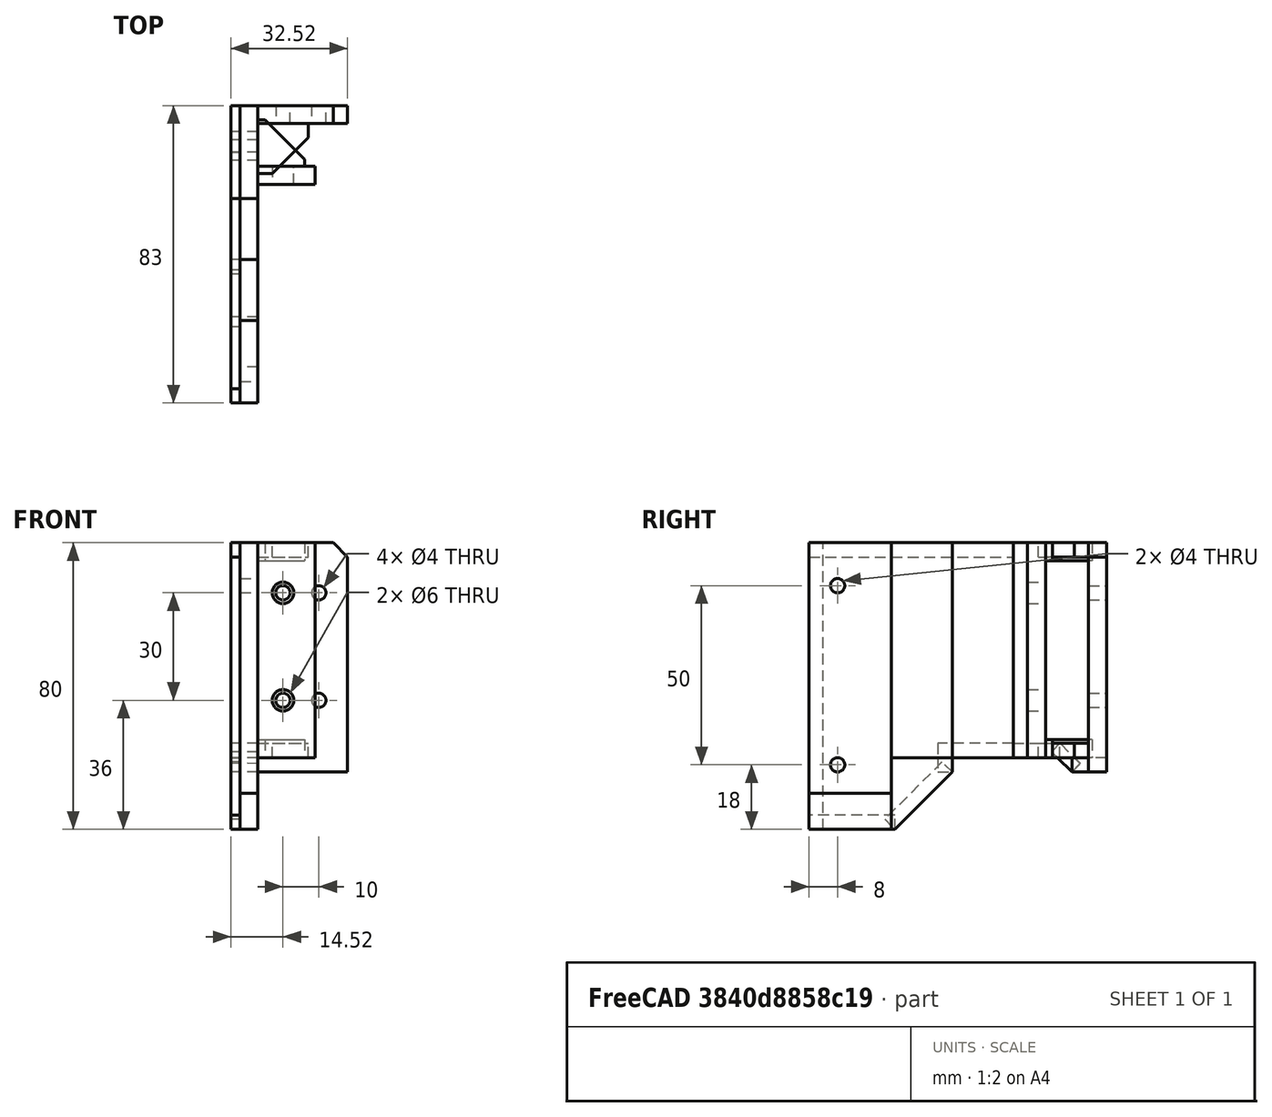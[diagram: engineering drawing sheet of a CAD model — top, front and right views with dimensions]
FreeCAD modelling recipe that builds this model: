
FCSTD DOCUMENT  (FreeCAD 0.20R29410 (Git))
Label: main_02
License: All rights reserved
LicenseURL: http://en.wikipedia.org/wiki/All_rights_reserved
objects: Part::Part2DObjectPython×35, Part::Extrusion×30, Part::Mirroring×22, Part::Cut×8, Part::Chamfer×6, App::FeaturePython×1
note: 101 computed .brp shape members not serialized (recipe doc carries the construction recipe); baked Part::Feature solids carry a one-line shape summary decoded from their .brp

FEATURE [Part::Part2DObjectPython] Rectangle  # Draft 2D object (typed FeaturePython)
  Area = 0
  ChamferSize = 0
  Columns = 1
  FilletRadius = 0
  Height = 70
  Length = 23
  MakeFace = false
  Placement = pos=(0,-40,0) rot=(0.57735,0.57735,0.57735;2.0944rad)
  Rows = 1
FEATURE [Part::Part2DObjectPython] Circle  # Draft 2D object (typed FeaturePython)
  Area = 0
  FirstAngle = 0
  LastAngle = 0
  MakeFace = false
  Placement = pos=(0,-32,58) rot=(0.57735,0.57735,0.57735;2.0944rad)
  Radius = 4
FEATURE [Part::Part2DObjectPython] Circle001  # Draft 2D object (typed FeaturePython)
  Area = 0
  FirstAngle = 0
  LastAngle = 0
  MakeFace = false
  Placement = pos=(0,-32,8) rot=(0.57735,0.57735,0.57735;2.0944rad)
  Radius = 4
FEATURE [Part::Part2DObjectPython] Rectangle001  # Draft 2D object (typed FeaturePython)
  Area = 0
  ChamferSize = 0
  Columns = 1
  FilletRadius = 0
  Height = 10
  Length = 23
  MakeFace = false
  Placement = pos=(0,-40,-10) rot=(0.57735,0.57735,0.57735;2.0944rad)
  Rows = 1
FEATURE [Part::Part2DObjectPython] Rectangle002  # Draft 2D object (typed FeaturePython)
  Area = 0
  ChamferSize = 0
  Columns = 1
  FilletRadius = 0
  Height = 20
  Length = 17
  MakeFace = false
  Placement = pos=(0,-17,-10) rot=(0.57735,0.57735,0.57735;2.0944rad)
  Rows = 1
FEATURE [Part::Part2DObjectPython] Rectangle003  # Draft 2D object (typed FeaturePython)
  Area = 0
  ChamferSize = 0
  Columns = 1
  FilletRadius = 0
  Height = 60
  Length = 17
  MakeFace = false
  Placement = pos=(0,0,10) rot=(0.57735,0.57735,0.57735;2.0944rad)
  Rows = 1
FEATURE [Part::Part2DObjectPython] Rectangle004  # Draft 2D object (typed FeaturePython)
  Area = 0
  ChamferSize = 0
  Columns = 1
  FilletRadius = 0
  Height = 60
  Length = 17
  MakeFace = false
  Placement = pos=(0,-17,10) rot=(0.57735,0.57735,0.57735;2.0944rad)
  Rows = 1
FEATURE [Part::Extrusion] Extrude
  Base = -> Rectangle
  Dir = (1,-2e-16,2e-16)
  DirMode = 2
  FaceMakerClass = Part::FaceMakerBullseye
  LengthFwd = 5
  LengthRev = 0
  Solid = true
  Symmetric = false
FEATURE [Part::Extrusion] Extrude001
  Base = -> Rectangle004
  Dir = (1,0,0)
  DirMode = 2
  FaceMakerClass = Part::FaceMakerBullseye
  LengthFwd = 5
  LengthRev = 0
  Solid = true
  Symmetric = false
FEATURE [Part::Extrusion] Extrude002
  Base = -> Rectangle003
  Dir = (1,-2e-16,2e-16)
  DirMode = 2
  FaceMakerClass = Part::FaceMakerBullseye
  LengthFwd = 5
  LengthRev = 0
  Solid = true
  Symmetric = false
FEATURE [Part::Extrusion] Extrude003
  Base = -> Rectangle001
  Dir = (1,-2e-16,2e-16)
  DirMode = 2
  FaceMakerClass = Part::FaceMakerBullseye
  LengthFwd = 5
  LengthRev = 0
  Solid = true
  Symmetric = false
FEATURE [Part::Extrusion] Extrude004
  Base = -> Rectangle002
  Dir = (1,-2e-16,2e-16)
  DirMode = 2
  FaceMakerClass = Part::FaceMakerBullseye
  LengthFwd = 5
  LengthRev = 0
  Solid = true
  Symmetric = false
FEATURE [Part::Chamfer] Chamfer
  Base = -> Extrude004
  Edges = 1 edges r=16: [Edge2]
FEATURE [Part::Part2DObjectPython] Rectangle005  # Draft 2D object (typed FeaturePython)
  Area = 0
  ChamferSize = 0
  Columns = 1
  FilletRadius = 0
  Height = 4
  Length = 57
  MakeFace = false
  Placement = pos=(5,-40,66) rot=(0.57735,0.57735,0.57735;2.0944rad)
  Rows = 1
FEATURE [Part::Part2DObjectPython] Rectangle006  # Draft 2D object (typed FeaturePython)
  Area = 0
  ChamferSize = 0
  Columns = 1
  FilletRadius = 0
  Height = 80
  Length = 4
  MakeFace = false
  Placement = pos=(5,-40,-10) rot=(0.57735,0.57735,0.57735;2.0944rad)
  Rows = 1
FEATURE [Part::Part2DObjectPython] Rectangle007  # Draft 2D object (typed FeaturePython)
  Area = 0
  ChamferSize = 0
  Columns = 1
  FilletRadius = 0
  Height = 4
  Length = 24
  MakeFace = false
  Placement = pos=(5,-40,-10) rot=(0.57735,0.57735,0.57735;2.0944rad)
  Rows = 1
FEATURE [Part::Part2DObjectPython] Rectangle008  # Draft 2D object (typed FeaturePython)
  Area = 0
  ChamferSize = 0
  Columns = 1
  FilletRadius = 0
  Height = 4
  Length = 22.6
  MakeFace = false
  Placement = pos=(5,-16,-10) rot=(0.678598,0.281085,0.678598;2.59356rad)
  Rows = 1
FEATURE [Part::Part2DObjectPython] Rectangle009  # Draft 2D object (typed FeaturePython)
  Area = 0
  ChamferSize = 0
  Columns = 1
  FilletRadius = 0
  Height = 4
  Length = 4
  MakeFace = false
  Placement = pos=(5,-4,6) rot=(0.57735,0.57735,0.57735;2.0944rad)
  Rows = 1
FEATURE [Part::Part2DObjectPython] Rectangle010  # Draft 2D object (typed FeaturePython)
  Area = 0
  ChamferSize = 0
  Columns = 1
  FilletRadius = 0
  Height = 4
  Length = 21
  MakeFace = false
  Placement = pos=(5,-4,10) rot=(0.57735,0.57735,0.57735;2.0944rad)
  Rows = 1
FEATURE [Part::Extrusion] Extrude005
  Base = -> Rectangle005
  Dir = (1,-2e-16,2e-16)
  DirMode = 2
  FaceMakerClass = Part::FaceMakerBullseye
  LengthFwd = 2.5
  LengthRev = 0
  Solid = true
  Symmetric = false
FEATURE [Part::Extrusion] Extrude006
  Base = -> Rectangle006
  Dir = (1,-2e-16,2e-16)
  DirMode = 2
  FaceMakerClass = Part::FaceMakerBullseye
  LengthFwd = 2.5
  LengthRev = 0
  Solid = true
  Symmetric = false
FEATURE [Part::Extrusion] Extrude007
  Base = -> Rectangle007
  Dir = (1,-2e-16,2e-16)
  DirMode = 2
  FaceMakerClass = Part::FaceMakerBullseye
  LengthFwd = 2.5
  LengthRev = 0
  Solid = true
  Symmetric = false
FEATURE [Part::Extrusion] Extrude008
  Base = -> Rectangle008
  Dir = (1,-2.79271e-06,1.15679e-06)
  DirMode = 2
  FaceMakerClass = Part::FaceMakerBullseye
  LengthFwd = 2.5
  LengthRev = 0
  Solid = true
  Symmetric = false
FEATURE [Part::Extrusion] Extrude009
  Base = -> Rectangle009
  Dir = (1,-2e-16,2e-16)
  DirMode = 2
  FaceMakerClass = Part::FaceMakerBullseye
  LengthFwd = 2.5
  LengthRev = 0
  Solid = true
  Symmetric = false
FEATURE [Part::Extrusion] Extrude010
  Base = -> Rectangle010
  Dir = (1,-2e-16,2e-16)
  DirMode = 2
  FaceMakerClass = Part::FaceMakerBullseye
  LengthFwd = 2.5
  LengthRev = 0
  Solid = true
  Symmetric = false
FEATURE [Part::Part2DObjectPython] Rectangle011  # Draft 2D object (typed FeaturePython)
  Area = 0
  ChamferSize = 0
  Columns = 1
  FilletRadius = 0
  Height = 60
  Length = 5.00266
  MakeFace = false
  Placement = pos=(6e-15,-13,10) rot=(0.57735,-0.57735,-0.57735;2.0944rad)
  Rows = 1
FEATURE [Part::Extrusion] Extrude011
  Base = -> Rectangle011
  Dir = (-1,2e-16,-2e-16)
  DirMode = 2
  FaceMakerClass = Part::FaceMakerBullseye
  LengthFwd = 16
  LengthRev = 0
  Placement = pos=(0,37,0) rot=(0,0,1;0rad)
  Solid = true
  Symmetric = false
FEATURE [Part::Part2DObjectPython] Rectangle012  # Draft 2D object (typed FeaturePython)
  Area = 0
  ChamferSize = 0
  Columns = 1
  FilletRadius = 0
  Height = 5
  Length = 13
  MakeFace = false
  Placement = pos=(0,0,63) rot=(0.57735,-0.57735,-0.57735;2.0944rad)
  Rows = 1
FEATURE [Part::Extrusion] Extrude012
  Base = -> Rectangle012
  Dir = (-1,-2e-16,2e-16)
  DirMode = 2
  FaceMakerClass = Part::FaceMakerBullseye
  LengthFwd = 13
  LengthRev = 0
  Solid = true
  Symmetric = false
FEATURE [Part::Chamfer] Chamfer001
  Base = -> Extrude012
  Edges = 1 edges r=11: [Edge12]
  Placement = pos=(0,39,2) rot=(0,0,1;0rad)
FEATURE [Part::Part2DObjectPython] Rectangle013  # Draft 2D object (typed FeaturePython)
  Area = 0
  ChamferSize = 0
  Columns = 1
  FilletRadius = 0
  Height = 5
  Length = 13
  MakeFace = false
  Placement = pos=(0,0,63) rot=(0.57735,-0.57735,-0.57735;2.0944rad)
  Rows = 1
FEATURE [Part::Extrusion] Extrude013
  Base = -> Rectangle013
  Dir = (-1,-2e-16,2e-16)
  DirMode = 2
  FaceMakerClass = Part::FaceMakerBullseye
  LengthFwd = 13
  LengthRev = 0
  Solid = true
  Symmetric = false
FEATURE [Part::Chamfer] Chamfer002
  Base = -> Extrude013
  Edges = 1 edges r=11: [Edge12]
  Placement = pos=(0,39,-53) rot=(0,0,1;0rad)
FEATURE [Part::Part2DObjectPython] Rectangle014  # Draft 2D object (typed FeaturePython)
  Area = 0
  ChamferSize = 0
  Columns = 1
  FilletRadius = 0
  Height = 49.9966
  Length = 4
  MakeFace = false
  Placement = pos=(0,-9,15) rot=(0.57735,-0.57735,-0.57735;2.0944rad)
  Rows = 1
FEATURE [Part::Part2DObjectPython] Rectangle015  # Draft 2D object (typed FeaturePython)
  Area = 0
  ChamferSize = 0
  Columns = 1
  FilletRadius = 0
  Height = 16
  Length = 5
  MakeFace = false
  Placement = pos=(0,-13,-6) rot=(0.57735,-0.57735,-0.57735;2.0944rad)
  Rows = 1
FEATURE [Part::Part2DObjectPython] Circle002  # Draft 2D object (typed FeaturePython)
  Area = 0
  FirstAngle = 0
  LastAngle = 0
  MakeFace = false
  Placement = pos=(0,-32,58) rot=(0.57735,0.57735,0.57735;2.0944rad)
  Radius = 2
FEATURE [Part::Part2DObjectPython] Circle003  # Draft 2D object (typed FeaturePython)
  Area = 0
  FirstAngle = 0
  LastAngle = 0
  MakeFace = false
  Placement = pos=(0,-32,8) rot=(0.57735,0.57735,0.57735;2.0944rad)
  Radius = 2
FEATURE [Part::Extrusion] Extrude016
  Base = -> Circle003
  Dir = (1,0,0)
  DirMode = 2
  FaceMakerClass = Part::FaceMakerBullseye
  LengthFwd = 5
  LengthRev = 0
  Solid = true
  Symmetric = false
FEATURE [Part::Extrusion] Extrude017
  Base = -> Circle002
  Dir = (1,0,0)
  DirMode = 2
  FaceMakerClass = Part::FaceMakerBullseye
  LengthFwd = 5
  LengthRev = 0
  Solid = true
  Symmetric = false
FEATURE [Part::Cut] Cut
  Base = -> Extrude
  Tool = -> Extrude016
FEATURE [Part::Cut] Cut001
  Base = -> Cut
  Tool = -> Extrude017
FEATURE [Part::Part2DObjectPython] Rectangle016  # Draft 2D object (typed FeaturePython)
  Area = 300
  ChamferSize = 0
  Columns = 1
  FilletRadius = 0
  Height = 60
  Length = 5
  MakeFace = true
  Placement = pos=(5,17,10) rot=(0,0.707107,0.707107;3.14159rad)
  Rows = 1
FEATURE [Part::Extrusion] Extrude018
  Base = -> Rectangle016
  Dir = (1e-16,1,0)
  DirMode = 2
  FaceMakerClass = Part::FaceMakerBullseye
  LengthFwd = 26
  LengthRev = 0
  Solid = false
  Symmetric = false
FEATURE [Part::Part2DObjectPython] Rectangle017  # Draft 2D object (typed FeaturePython)
  Area = 10
  ChamferSize = 0
  Columns = 1
  FilletRadius = 0
  Height = 4
  Length = 2.5
  MakeFace = true
  Placement = pos=(7.5,17,66) rot=(0,0.707107,0.707107;3.14159rad)
  Rows = 1
FEATURE [Part::Part2DObjectPython] Rectangle018  # Draft 2D object (typed FeaturePython)
  Area = 10
  ChamferSize = 0
  Columns = 1
  FilletRadius = 0
  Height = 4
  Length = 2.5
  MakeFace = true
  Placement = pos=(7.5,17,10) rot=(0,0.707107,0.707107;3.14159rad)
  Rows = 1
FEATURE [Part::Extrusion] Extrude019
  Base = -> Rectangle017
  Dir = (2e-16,1,-2e-16)
  DirMode = 2
  FaceMakerClass = Part::FaceMakerBullseye
  LengthFwd = 26
  LengthRev = 0
  Solid = false
  Symmetric = false
FEATURE [Part::Extrusion] Extrude020
  Base = -> Rectangle018
  Dir = (1e-16,1,0)
  DirMode = 2
  FaceMakerClass = Part::FaceMakerBullseye
  LengthFwd = 13
  LengthRev = 0
  Solid = false
  Symmetric = false
FEATURE [Part::Part2DObjectPython] Rectangle019  # Draft 2D object (typed FeaturePython)
  Area = 38.4
  ChamferSize = 0
  Columns = 1
  FilletRadius = 0
  Height = 4
  Length = 9.6
  MakeFace = true
  Placement = pos=(5,33.4,6) rot=(0.57735,0.57735,0.57735;2.0944rad)
  Rows = 1
FEATURE [Part::Part2DObjectPython] Rectangle020  # Draft 2D object (typed FeaturePython)
  Area = 26.4
  ChamferSize = 0
  Columns = 1
  FilletRadius = 0
  Height = 3.3
  Length = 8
  MakeFace = true
  Placement = pos=(5,27.7,11.65) rot=(0.360216,0.860516,0.360216;1.71775rad)
  Rows = 1
FEATURE [Part::Extrusion] Extrude021
  Base = -> Rectangle020
  Dir = (0.999997,-0.000972878,0.00232728)
  DirMode = 2
  FaceMakerClass = Part::FaceMakerBullseye
  LengthFwd = 2.5
  LengthRev = 5
  Solid = false
  Symmetric = false
FEATURE [Part::Extrusion] Extrude022
  Base = -> Rectangle019
  Dir = (1,-2e-16,2e-16)
  DirMode = 2
  FaceMakerClass = Part::FaceMakerBullseye
  LengthFwd = 2.5
  LengthRev = 5
  Solid = false
  Symmetric = false
FEATURE [Part::Part2DObjectPython] Rectangle021  # Draft 2D object (typed FeaturePython)
  Area = 320
  ChamferSize = 0
  Columns = 1
  FilletRadius = 0
  Height = 64
  Length = 5
  MakeFace = true
  Placement = pos=(0,38,6) rot=(0.57735,0.57735,0.57735;2.0944rad)
  Rows = 1
FEATURE [Part::Extrusion] Extrude023
  Base = -> Rectangle021
  Dir = (1,-2e-16,2e-16)
  DirMode = 2
  FaceMakerClass = Part::FaceMakerBullseye
  LengthFwd = -25
  LengthRev = 0
  Solid = false
  Symmetric = false
FEATURE [Part::Chamfer] Chamfer005
  Base = -> Extrude023
  Edges = 1 edges r=4: [Edge10]
FEATURE [Part::Part2DObjectPython] Rectangle022  # Draft 2D object (typed FeaturePython)
  Area = 56
  ChamferSize = 0
  Columns = 1
  FilletRadius = 0
  Height = 4
  Length = 14
  MakeFace = true
  Placement = pos=(0,38,66) rot=(0.57735,-0.57735,-0.57735;2.0944rad)
  Rows = 1
FEATURE [Part::Extrusion] Extrude024
  Base = -> Rectangle022
  Dir = (-1,2e-16,-2e-16)
  DirMode = 2
  FaceMakerClass = Part::FaceMakerBullseye
  LengthFwd = 14
  LengthRev = 0
  Solid = false
  Symmetric = false
FEATURE [Part::Chamfer] Chamfer006
  Base = -> Extrude024
  Edges = 1 edges r=10: [Edge7]
FEATURE [Part::Part2DObjectPython] Rectangle023  # Draft 2D object (typed FeaturePython)
  Area = 56
  ChamferSize = 0
  Columns = 1
  FilletRadius = 0
  Height = 4
  Length = 14
  MakeFace = true
  Placement = pos=(0,38,66) rot=(0.57735,-0.57735,-0.57735;2.0944rad)
  Rows = 1
FEATURE [Part::Extrusion] Extrude025
  Base = -> Rectangle023
  Dir = (-1,2e-16,-2e-16)
  DirMode = 2
  FaceMakerClass = Part::FaceMakerBullseye
  LengthFwd = 14
  LengthRev = 0
  Solid = false
  Symmetric = false
FEATURE [Part::Chamfer] Chamfer007
  Base = -> Extrude025
  Edges = 1 edges r=10: [Edge7]
  Placement = pos=(0,0,-56) rot=(0,0,1;0rad)
FEATURE [Part::Part2DObjectPython] Rectangle071  # Draft 2D object (typed FeaturePython)
  Area = 140
  ChamferSize = 0
  Columns = 1
  FilletRadius = 0
  Height = 20
  Length = 7
  MakeFace = true
  Placement = pos=(-7,43,6) rot=(1,0,0;1.5708rad)
  Rows = 1
FEATURE [Part::Part2DObjectPython] Circle004  # Draft 2D object (typed FeaturePython)
  Area = 12.5664
  FirstAngle = 0
  LastAngle = 0
  MakeFace = true
  Placement = pos=(-17,43,26) rot=(1,0,0;1.5708rad)
  Radius = 2
FEATURE [Part::Part2DObjectPython] Circle005  # Draft 2D object (typed FeaturePython)
  Area = 12.5664
  FirstAngle = 0
  LastAngle = 0
  MakeFace = true
  Placement = pos=(-17,43,56) rot=(1,0,0;1.5708rad)
  Radius = 2
FEATURE [Part::Part2DObjectPython] Circle006  # Draft 2D object (typed FeaturePython)
  Area = 12.5664
  FirstAngle = 0
  LastAngle = 0
  MakeFace = true
  Placement = pos=(-7,43,56) rot=(1,0,0;1.5708rad)
  Radius = 2
FEATURE [Part::Part2DObjectPython] Circle007  # Draft 2D object (typed FeaturePython)
  Area = 12.5664
  FirstAngle = 0
  LastAngle = 0
  MakeFace = true
  Placement = pos=(-7,43,26) rot=(1,0,0;1.5708rad)
  Radius = 2
FEATURE [Part::Extrusion] Extrude026
  Base = -> Circle004
  Dir = (0,-1,2e-16)
  DirMode = 2
  FaceMakerClass = Part::FaceMakerBullseye
  LengthFwd = 5
  LengthRev = 0
  Solid = false
  Symmetric = false
FEATURE [Part::Extrusion] Extrude027
  Base = -> Circle007
  Dir = (0,-1,2e-16)
  DirMode = 2
  FaceMakerClass = Part::FaceMakerBullseye
  LengthFwd = 5
  LengthRev = 0
  Solid = false
  Symmetric = false
FEATURE [Part::Extrusion] Extrude028
  Base = -> Circle006
  Dir = (0,-1,2e-16)
  DirMode = 2
  FaceMakerClass = Part::FaceMakerBullseye
  LengthFwd = 5
  LengthRev = 0
  Solid = false
  Symmetric = false
FEATURE [Part::Extrusion] Extrude029
  Base = -> Circle005
  Dir = (0,-1,2e-16)
  DirMode = 2
  FaceMakerClass = Part::FaceMakerBullseye
  LengthFwd = 5
  LengthRev = 0
  Solid = false
  Symmetric = false
FEATURE [Part::Cut] Cut002
  Base = -> Chamfer005
  Tool = -> Extrude026
FEATURE [Part::Cut] Cut003
  Base = -> Cut002
  Tool = -> Extrude027
FEATURE [Part::Cut] Cut004
  Base = -> Cut003
  Tool = -> Extrude028
FEATURE [Part::Cut] Cut005
  Base = -> Cut004
  Tool = -> Extrude029
FEATURE [Part::Mirroring] Part__Mirroring  label="Extrude001 (Mirror #1)"
  Base = (30,0,0)
  Normal = (1,0,0)
  Source = -> Extrude001
FEATURE [Part::Mirroring] Part__Mirroring001  label="Extrude002 (Mirror #2)"
  Base = (30,0,0)
  Normal = (1,0,0)
  Source = -> Extrude002
FEATURE [Part::Mirroring] Part__Mirroring002  label="Extrude003 (Mirror #3)"
  Base = (30,0,0)
  Normal = (1,0,0)
  Source = -> Extrude003
FEATURE [Part::Mirroring] Part__Mirroring003  label="Chamfer (Mirror #4)"
  Base = (30,0,0)
  Normal = (1,0,0)
  Source = -> Chamfer
FEATURE [Part::Mirroring] Part__Mirroring004  label="Extrude005 (Mirror #5)"
  Base = (30,0,0)
  Normal = (1,0,0)
  Source = -> Extrude005
FEATURE [Part::Mirroring] Part__Mirroring005  label="Extrude006 (Mirror #6)"
  Base = (30,0,0)
  Normal = (1,0,0)
  Source = -> Extrude006
FEATURE [Part::Mirroring] Part__Mirroring006  label="Extrude007 (Mirror #7)"
  Base = (30,0,0)
  Normal = (1,0,0)
  Source = -> Extrude007
FEATURE [Part::Mirroring] Part__Mirroring007  label="Extrude008 (Mirror #8)"
  Base = (30,0,0)
  Normal = (1,0,0)
  Source = -> Extrude008
FEATURE [Part::Mirroring] Part__Mirroring008  label="Extrude009 (Mirror #9)"
  Base = (30,0,0)
  Normal = (1,0,0)
  Source = -> Extrude009
FEATURE [Part::Mirroring] Part__Mirroring009  label="Extrude010 (Mirror #10)"
  Base = (30,0,0)
  Normal = (1,0,0)
  Source = -> Extrude010
FEATURE [Part::Mirroring] Part__Mirroring011  label="Chamfer001 (Mirror #12)"
  Base = (30,0,0)
  Normal = (1,0,0)
  Source = -> Chamfer001
FEATURE [Part::Mirroring] Part__Mirroring012  label="Chamfer002 (Mirror #13)"
  Base = (30,0,0)
  Normal = (1,0,0)
  Source = -> Chamfer002
FEATURE [Part::Mirroring] Part__Mirroring015  label="Cut001 (Mirror #16)"
  Base = (30,0,0)
  Normal = (1,0,0)
  Source = -> Cut001
FEATURE [Part::Mirroring] Part__Mirroring016  label="Extrude018 (Mirror #17)"
  Base = (30,0,0)
  Normal = (1,0,0)
  Source = -> Extrude018
FEATURE [Part::Mirroring] Part__Mirroring017  label="Extrude019 (Mirror #18)"
  Base = (30,0,0)
  Normal = (1,0,0)
  Source = -> Extrude019
FEATURE [Part::Mirroring] Part__Mirroring018  label="Extrude020 (Mirror #19)"
  Base = (30,0,0)
  Normal = (1,0,0)
  Source = -> Extrude020
FEATURE [Part::Mirroring] Part__Mirroring019  label="Extrude021 (Mirror #20)"
  Base = (30,0,0)
  Normal = (1,0,0)
  Source = -> Extrude021
FEATURE [Part::Mirroring] Part__Mirroring020  label="Extrude022 (Mirror #21)"
  Base = (30,0,0)
  Normal = (1,0,0)
  Source = -> Extrude022
FEATURE [Part::Mirroring] Part__Mirroring021  label="Chamfer006 (Mirror #22)"
  Base = (30,0,0)
  Normal = (1,0,0)
  Source = -> Chamfer006
FEATURE [Part::Mirroring] Part__Mirroring022  label="Chamfer007 (Mirror #23)"
  Base = (30,0,0)
  Normal = (1,0,0)
  Source = -> Chamfer007
FEATURE [Part::Mirroring] Part__Mirroring023  label="Cut005 (Mirror #24)"
  Base = (30,0,0)
  Normal = (1,0,0)
  Source = -> Cut005
FEATURE [Part::Part2DObjectPython] Circle008  # Draft 2D object (typed FeaturePython)
  Area = 28.2743
  FirstAngle = 0
  LastAngle = 0
  MakeFace = true
  Placement = pos=(-7,24,56) rot=(1,0,0;1.5708rad)
  Radius = 3
FEATURE [Part::Part2DObjectPython] Circle009  # Draft 2D object (typed FeaturePython)
  Area = 28.2743
  FirstAngle = 0
  LastAngle = 0
  MakeFace = true
  Placement = pos=(-7,24,26) rot=(1,0,0;1.5708rad)
  Radius = 3
FEATURE [Part::Extrusion] Extrude030
  Base = -> Circle008
  Dir = (0,-1,2e-16)
  DirMode = 2
  FaceMakerClass = Part::FaceMakerBullseye
  LengthFwd = 10
  LengthRev = 0
  Solid = false
  Symmetric = false
FEATURE [Part::Extrusion] Extrude031
  Base = -> Circle009
  Dir = (0,-1,2e-16)
  DirMode = 2
  FaceMakerClass = Part::FaceMakerBullseye
  LengthFwd = 10
  LengthRev = 0
  Solid = false
  Symmetric = false
FEATURE [Part::Cut] Cut006
  Base = -> Extrude011
  Tool = -> Extrude030
FEATURE [Part::Cut] Cut007
  Base = -> Cut006
  Placement = pos=(0,2,0) rot=(0,0,1;0rad)
  Tool = -> Extrude031
FEATURE [Part::Mirroring] Part__Mirroring024  label="Cut007 (Mirror #22)"
  Base = (30,0,0)
  Normal = (1,0,0)
  Source = -> Cut007
FEATURE [App::FeaturePython] Text  # WARN: FeaturePython — macro-defined, semantics opaque (R4)
  Placement = pos=(68,-68.2,4.71) rot=(0.57735,0.57735,0.57735;2.0944rad)
  Text = USE THIS ONE (RIGHT)
